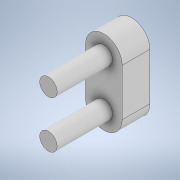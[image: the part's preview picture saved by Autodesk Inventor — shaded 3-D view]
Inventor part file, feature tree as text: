
AUTODESK INVENTOR PART (.ipt)
format: ipt  version: 2022 (Build 260153000, 153)  size: 120,832 bytes
history: native  units: in
note: dims shown in document units (in); Inventor stores cm internally (conversion verified against a paired STEP export)
features: extrude x2, sketch x2, other x1
ambient origin geometry x8: Origin, YZ Plane, XZ Plane, XY Plane, X Axis, Y Axis, Z Axis, Center Point
bodies: Body1 (feature_tree)
feature tree (5):
  other  "Sólido1"
  extrude  "Extrusión1"  Depth=0.0984in
  extrude  "Extrusión2"  Depth=0.4724in TaperAngle=0.0deg
  sketch  "Boceto1"  dims[d0=0.0984in d1=0.0984in]
  sketch  "Boceto2"  dims[d2=0.1575in d3=0.0in d4=0.4724in d5=0.0in d6=0.1039in d7=0.1039in d8=0.2677in d9=0.2077in]
